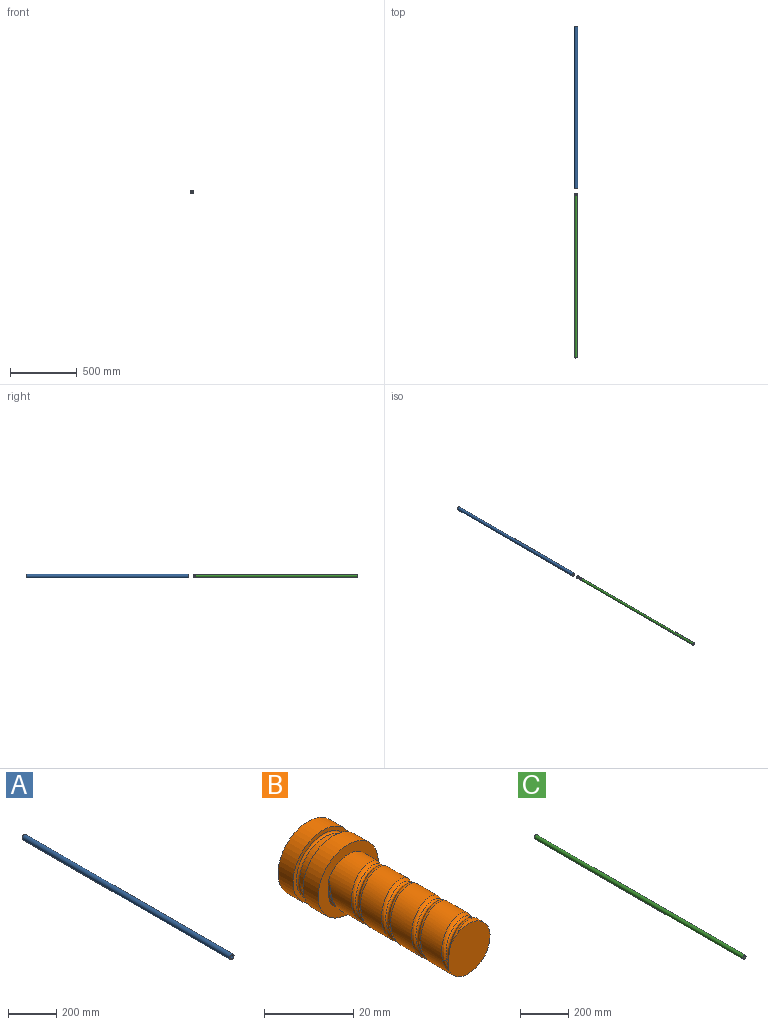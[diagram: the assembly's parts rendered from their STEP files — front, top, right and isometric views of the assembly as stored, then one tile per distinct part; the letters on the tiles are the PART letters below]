
ASSEMBLY  parts=3 mates=3
PART A: 4 faces, bbox 25.4x1219.2x25.4 mm
  f0: cylinder r=10.16mm len=1219.2mm, axis (0,1,0), area 77830.3mm2, adj f2,f3
  f1: cylinder r=12.7mm len=1219.2mm, axis (0,1,0), area 97287.8mm2, adj f2,f3
  f2: plane 25.4x25.4mm, normal (0,-1,0), area 182.4mm2, adj f0,f1
  f3: plane 25.4x25.4mm, normal (0,1,0), area 182.4mm2, adj f0,f1
PART B: 18 faces, bbox 19.2x53x19.2 mm
  f0: cylinder r=6.86mm len=38.1mm, axis (0,1,0), area 1140.1mm2, adj f1,f5,f6,f7,f8,f9
  f1: plane 13.86x13.36mm, normal (0,-1,0), area 144.9mm2, adj f0,f2,f4,f6,f7
  f2: bspline ~42.2x13.93mm, area 171.5mm2, adj f1,f3,f4,f5,f6,f7,f8,f9
  f3: cylinder r=0.64mm len=1.69mm, axis (0,-0.22,-0.98), area 0.4mm2, adj f2,f8,f9
  f4: cylinder r=0.64mm len=1.69mm, axis (0,0.22,0.98), area 0.4mm2, adj f1,f2,f6
  f5: bspline ~38.73x13.74mm, area 181.6mm2, adj f0,f2,f6,f9
  f6: bspline ~3.38x1.87mm, area 2.4mm2, adj f0,f1,f2,f4,f5
  f7: bspline ~38.73x13.74mm, area 181.6mm2, adj f0,f1,f2,f8
  f8: bspline ~3.19x1.86mm, area 2.4mm2, adj f0,f2,f3,f7,f9
  f9: plane 19.19x19.19mm, normal (0,-1,0), area 140.1mm2, adj f0,f2,f3,f5,f8,f10
  f10: cylinder r=9.53mm len=19.05mm, axis (0,-1,0), area 285mm2, adj f9,f12
  f11: plane 19.05x19.05mm, normal (0,-1,0), area 60.9mm2, adj f15,f17
  f12: plane 19.05x19.05mm, normal (0,1,0), area 60.9mm2, adj f10,f16
  f13: cylinder r=7.94mm len=15.88mm, axis (0,1,0), area 107.7mm2, adj f16,f17
  f14: plane 19.05x19.05mm, normal (0,1,0), area 285mm2, adj f15
  f15: cylinder r=9.53mm len=19.05mm, axis (0,-1,0), area 285mm2, adj f11,f14
  f16: torus R=8.45mm, axis (0,-1,0), area 40.7mm2, adj f12,f13
  f17: torus R=8.45mm, axis (0,-1,0), area 40.7mm2, adj f11,f13
PART C: 4 faces, bbox 19.1x1219.2x19.1 mm
  f0: cylinder r=6.99mm len=1219.2mm, axis (0,1,0), area 53508.3mm2, adj f2,f3
  f1: cylinder r=9.53mm len=1219.2mm, axis (0,1,0), area 72965.9mm2, adj f2,f3
  f2: plane 19.05x19.05mm, normal (0,-1,0), area 131.7mm2, adj f0,f1
  f3: plane 19.05x19.05mm, normal (0,1,0), area 131.7mm2, adj f0,f1
PLACE A at identity
PLACE B rot(axis=(0,1,0),11.9deg) t=(0,-1274.33,0)mm
PLACE C rot(axis=(0,1,0),24.7deg) t=(0,-1274.33,0)mm
MATE planar C.f1 <-> B.f10  axis (0,1,0) through (0,-1274.33,0)mm
MATE cylindrical B.f0 <-> C.f0  axis (0,1,0) through (0,-1293.38,0)mm
MATE cylindrical C.f1 <-> A.f0  axis (0,1,0) through (0,-1883.93,0)mm
